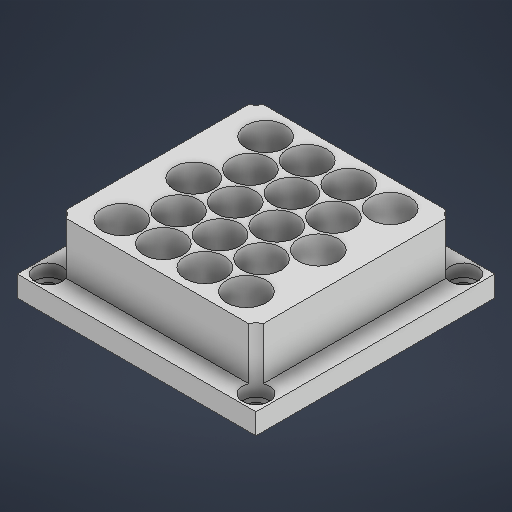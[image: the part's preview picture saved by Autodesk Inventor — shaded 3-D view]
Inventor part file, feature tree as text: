
AUTODESK INVENTOR PART (.ipt)
format: ipt  version: 2025 (Build 290162000, 162)  size: 311,296 bytes
history: native  units: in
note: dims shown in document units (in); Inventor stores cm internally (conversion verified against a paired STEP export)
features: sketch x6, extrude x2, hole x1
ambient origin geometry x8: Origin, YZ Plane, XZ Plane, XY Plane, X Axis, Y Axis, Z Axis, Center Point
bodies: Solid1 (feature_tree)
feature tree (9):
  extrude  "Extrusion1"  Depth=4.5276in
  extrude  "Extrusion2"  Depth=3.7402in
  hole  "Hole3"  [1 undecoded]
  sketch  "Sketch1"  dims[d0=4.5276in d1=4.5276in]
  sketch  "Sketch4"  dims[d2=0.3937in d3=0.0in d48=3.7402in]
  sketch  "Sketch Rectangular Pattern11"  dims[d124=1.3638in]
  sketch  "Sketch Rectangular Pattern12"  dims[d132=2.3622in]
  sketch  "Sketch5"  dims[d49=3.7402in d57=0.9843in d58=0.0in]
  sketch  "Sketch Rectangular Pattern13"  dims[d133=2.7276in d134=0.748in d135=1.5748in d137=0.7874in d138=1.1811in d140=1.3638in d143=0.748in d146=0.3937in d147=0.6819in d148=1.1811in d150=0.7874in d151=0.7874in d153=1.3638in d156=3.937in d157=3.937in d158=0.2756in d159=0.7874in d161=3.937in d162=0.7874in d164=3.937in d167=0.2805in d168=0.2362in d169=0.5118in d170=1.2205in d171=90.0deg d172=0.315in d173=0.8108in]
note: 1 required parameter value undecoded (feature->parameter linkage not recoverable at this tier; creation-order binding heuristic only, values carry confidence <= 0.55)
